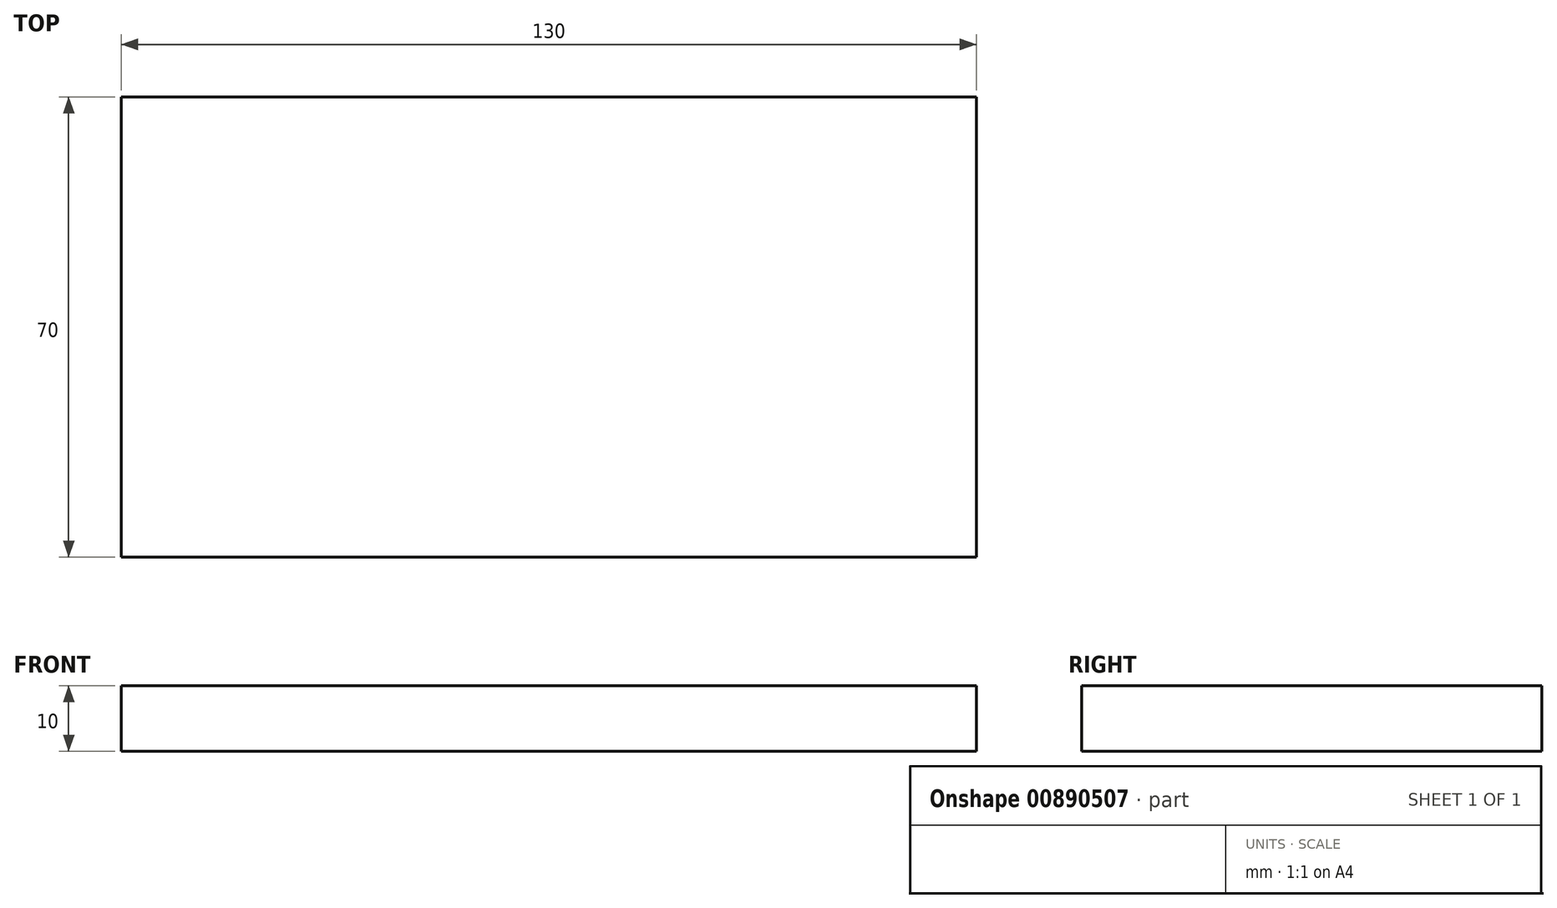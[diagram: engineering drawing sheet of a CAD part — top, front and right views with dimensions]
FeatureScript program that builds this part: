
annotation { "Feature Type Name" : "Feature", "Feature Type Description" : "" }
export const myFeature = defineFeature(function(context is Context, id is Id, definition is map)
    precondition{}
    {
        {
            var Q0;
            Q0=qCreatedBy(makeId("Top.planeOp"),FACE);
            var sketch = newSketch(context, id + "F0", { "sketchPlane" : qUnion([Q0])});
            skLineSegment(sketch, "E0.bottom", {"start": v(65, 35) * mm, "end": v(-65, 35) * mm});
            skLineSegment(sketch, "E0.top", {"start": v(65, -35) * mm, "end": v(-65, -35) * mm});
            skLineSegment(sketch, "E0.left", {"start": v(65, 35) * mm, "end": v(65, -35) * mm});
            skLineSegment(sketch, "E0.right", {"start": v(-65, 35) * mm, "end": v(-65, -35) * mm});
            skPoint(sketch, "E0.middle", {"position": v(0, 0) * mm});
            skSolve(sketch);
        }
        {
            var Q0;
            Q0=makeQuery(id+"F0.imprint","IMPRINT",FACE,{"disambiguationData":[TD([[makeQuery(id+"F0.imprint","IMPRINT",EDGE,{"derivedFrom":sQuery(id+"F0.wireOp",EDGE,"E0.bottom")}),1.0]])]});
            extrude(context, id + "F1", {"entities" : qUnion([Q0]), "depth" : 10 * mm, "offsetDistance" : 25 * mm});
        }
    });
